# Revit family: 53-42-001-DN80-150
name_source: partatom
category: Pipe Accessories
units: mm (PartAtom-declared; Revit-internal decimal feet)

## family parameters
Always vertical = Yes
Cut with Voids When Loaded = No
Part Type = Valve - Breaks Into
Round Connector Dimension = Use Diameter
Shared = No
Work Plane-Based = No

## types (3) — shared parameters
Body_Wall_thickness = 10 mm  [stored 0.0328084 ft]
DN = 80 mm  [stored 0.262467 ft]
DN100_PN10 = 53-100-42-1090
DN150_PN10 = 53-150-42-1090
DN80_PN10 = 53-080-42-1090
Description_ = AVK BALL CHECK VALVE, FLANGED
Ear_Height = 5 mm  [stored 0.0164042 ft]
Ear_width = 5 mm  [stored 0.0164042 ft]
Flange_Thickness = 18 mm  [stored 0.0590551 ft]
Hook_Distance = 10 mm  [stored 0.0328084 ft]
RF_Thickness = 3 mm  [stored 0.00984252 ft]
Search_table = 53-42-001-DN80-150
URL product pages = https://www.avkvalves.com

## per-type parameters (varying)
- DN080: Body_Height_1=50 mm  [stored 0.164042 ft]; Body_Height_2=105 mm; Body_Height_3=58 mm  [stored 0.190289 ft]; Body_Ref=108 mm; Body_distance_1=19 mm  [stored 0.062336 ft]; Body_distance_3=30 mm  [stored 0.0984252 ft]; Bottom_height=7.5 mm  [stored 0.0246063 ft]; Chamfer=22 mm  [stored 0.0721785 ft]; Chamfer_Ref=63 mm  [stored 0.206693 ft]; Circle_Height=35 mm  [stored 0.114829 ft]; Circle_Height_2=30 mm  [stored 0.0984252 ft]; Circle_Length=55 mm  [stored 0.180446 ft]; Circle_Radius_2=1779 mm; Circle_cut=2 mm  [stored 0.00656168 ft]; Circle_radius=63.5 mm; Cut_Height_Ref=98.67 mm; Cut_ref=50 mm  [stored 0.164042 ft]; Distance_1=13 mm  [stored 0.0426509 ft]; Distance_2=85 mm  [stored 0.278871 ft]; Distance_3=95 mm  [stored 0.31168 ft]; Distance_4=5 mm  [stored 0.0164042 ft]; Ear_Lenght_2=40 mm  [stored 0.131234 ft]; Ear_Length=80 mm  [stored 0.262467 ft]; Ear_Reference=103 mm; Ear_Reference_2=9 mm  [stored 0.0295276 ft]; F_OD=100 mm  [stored 0.328084 ft]; Fillet_Thickness_2=5 mm  [stored 0.0164042 ft]; Flange_Dia=63 mm  [stored 0.206693 ft]; Flange_Thickness_2=10 mm  [stored 0.0328084 ft]; H=148 mm; Hook_Distance_2=10 mm  [stored 0.0328084 ft]; Hook_Height=20 mm  [stored 0.0656168 ft]; Hook_Height_2=15 mm  [stored 0.0492126 ft]; Hook_Legnth=10 mm  [stored 0.0328084 ft]; ID=40 mm  [stored 0.131234 ft]; L=260 mm; L2=390 mm; Nominal_Diameter=80 mm  [stored 0.262467 ft]; RF=80 mm  [stored 0.262467 ft]; Rib_Distance=40 mm  [stored 0.131234 ft]; Rib_Distance_2=40 mm  [stored 0.131234 ft]; Rib_height=35 mm  [stored 0.114829 ft]
- DN100: Body_Height_1=60 mm  [stored 0.19685 ft]; Body_Height_2=100 mm  [stored 0.328084 ft]; Body_Height_3=73 mm  [stored 0.239501 ft]; Body_Ref=128 mm; Body_distance_1=21 mm  [stored 0.0688976 ft]; Body_distance_3=55 mm  [stored 0.180446 ft]; Bottom_height=10 mm  [stored 0.0328084 ft]; Chamfer=50 mm  [stored 0.164042 ft]; Chamfer_Ref=80 mm  [stored 0.262467 ft]; Circle_Height=35 mm  [stored 0.114829 ft]; Circle_Height_2=40 mm  [stored 0.131234 ft]; Circle_Length=60 mm  [stored 0.19685 ft]; Circle_Radius_2=1974 mm; Circle_cut=2 mm  [stored 0.00656168 ft]; Circle_radius=64 mm  [stored 0.209974 ft]; Cut_Height_Ref=121.33 mm; Cut_ref=60 mm  [stored 0.19685 ft]; Distance_1=17 mm  [stored 0.0557743 ft]; Distance_2=100 mm  [stored 0.328084 ft]; Distance_3=111 mm; Distance_4=28 mm  [stored 0.0918635 ft]; Ear_Lenght_2=50 mm  [stored 0.164042 ft]; Ear_Length=100 mm  [stored 0.328084 ft]; Ear_Reference=127 mm; Ear_Reference_2=33 mm  [stored 0.108268 ft]; F_OD=110 mm; Fillet_Thickness_2=5 mm  [stored 0.0164042 ft]; Flange_Dia=80 mm  [stored 0.262467 ft]; Flange_Thickness_2=11 mm  [stored 0.0360892 ft]; H=182 mm; Hook_Distance_2=5 mm  [stored 0.0164042 ft]; Hook_Height=25 mm  [stored 0.082021 ft]; Hook_Height_2=20 mm  [stored 0.0656168 ft]; Hook_Legnth=10 mm  [stored 0.0328084 ft]; ID=50 mm  [stored 0.164042 ft]; L=300 mm; L2=450 mm; Nominal_Diameter=100 mm  [stored 0.328084 ft]; RF=90 mm  [stored 0.295276 ft]; Rib_Distance=50 mm  [stored 0.164042 ft]; Rib_Distance_2=50 mm  [stored 0.164042 ft]; Rib_height=40 mm  [stored 0.131234 ft]
- DN150: Body_Height_1=85 mm  [stored 0.278871 ft]; Body_Height_2=120 mm; Body_Height_3=100 mm  [stored 0.328084 ft]; Body_Ref=160 mm; Body_distance_1=25 mm  [stored 0.082021 ft]; Body_distance_3=65 mm  [stored 0.213255 ft]; Bottom_height=10 mm  [stored 0.0328084 ft]; Chamfer=50 mm  [stored 0.164042 ft]; Chamfer_Ref=108 mm; Circle_Height=50 mm  [stored 0.164042 ft]; Circle_Height_2=60 mm  [stored 0.19685 ft]; Circle_Length=95 mm  [stored 0.31168 ft]; Circle_Radius_2=2268 mm; Circle_cut=5 mm  [stored 0.0164042 ft]; Circle_radius=115 mm; Cut_Height_Ref=167.33 mm; Cut_ref=85 mm  [stored 0.278871 ft]; Distance_1=5 mm  [stored 0.0164042 ft]; Distance_2=130 mm; Distance_3=155 mm; Distance_4=80 mm  [stored 0.262467 ft]; Ear_Lenght_2=70 mm  [stored 0.229659 ft]; Ear_Length=140 mm; Ear_Reference=176 mm; Ear_Reference_2=83 mm  [stored 0.27231 ft]; F_OD=142.5 mm; Fillet_Thickness_2=7 mm  [stored 0.0229659 ft]; Flange_Dia=108 mm; Flange_Thickness_2=11 mm  [stored 0.0360892 ft]; H=251 mm; Hook_Distance_2=10 mm  [stored 0.0328084 ft]; Hook_Height=30 mm  [stored 0.0984252 ft]; Hook_Height_2=15 mm  [stored 0.0492126 ft]; Hook_Legnth=20 mm  [stored 0.0656168 ft]; ID=75 mm; L=400 mm; L2=600 mm; Nominal_Diameter=150 mm; RF=104.5 mm; Rib_Distance=70 mm  [stored 0.229659 ft]; Rib_Distance_2=70 mm  [stored 0.229659 ft]; Rib_height=40 mm  [stored 0.131234 ft]

note: [stored X ft] marks values corroborated as IEEE doubles in the binary element streams (Revit-internal decimal feet)

## geometry (parser evidence)
native form markers: Sweep x5
no freeform markers — native parametric forms only
